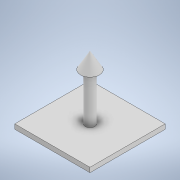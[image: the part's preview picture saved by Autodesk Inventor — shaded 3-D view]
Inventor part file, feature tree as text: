
AUTODESK INVENTOR PART (.ipt)
format: ipt  version: 2020 (Build 240168000, 168)  size: 112,640 bytes
history: native  units: in
note: dims shown in document units (in); Inventor stores cm internally (conversion verified against a paired STEP export)
features: extrude x3, sketch x3
ambient origin geometry x8: Origin, YZ Plane, XZ Plane, XY Plane, X Axis, Y Axis, Z Axis, Center Point
bodies: Solid1 (feature_tree)
feature tree (6):
  extrude  "Extrusion1"  Depth=0.25in
  extrude  "Extrusion2"  Depth=0.5in
  extrude  "Extrusion3"  Depth=2.5in
  sketch  "Sketch1"  dims[d0=4.0in d1=0.25in]
  sketch  "Sketch2"  dims[d2=4.0in d3=0.0in d4=0.5in]
  sketch  "Sketch3"  dims[d5=2.0in d6=2.0in d7=2.5in d8=0.0in d9=1.0in d10=1.0in d11=-0.2061in]
